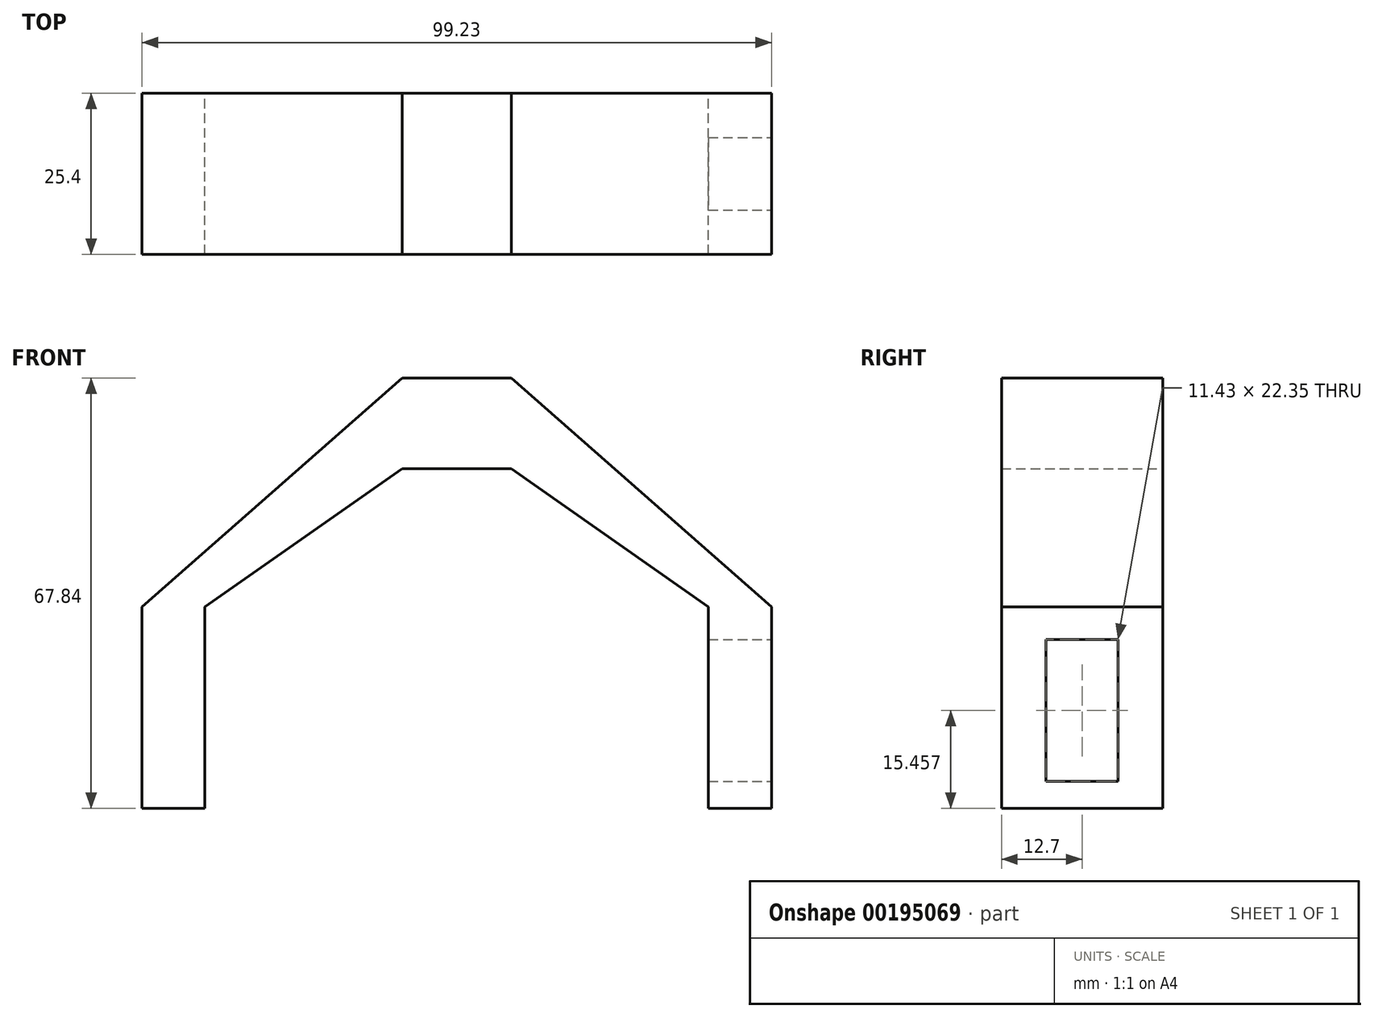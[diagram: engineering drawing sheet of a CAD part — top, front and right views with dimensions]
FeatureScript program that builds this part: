
annotation { "Feature Type Name" : "Feature", "Feature Type Description" : "" }
export const myFeature = defineFeature(function(context is Context, id is Id, definition is map)
    precondition{}
    {
        {
            var Q0;
            Q0=qCreatedBy(makeId("Front.planeOp"),FACE);
            var sketch = newSketch(context, id + "F0", { "sketchPlane" : qUnion([Q0])});
            skLineSegment(sketch, "E0.bottom", {"start": v(-126.2, 0) * mm, "end": v(-116.27, 0) * mm});
            skLineSegment(sketch, "E0.top", {"start": v(-126.2, 31.75) * mm, "end": v(-116.27, 31.75) * mm});
            skLineSegment(sketch, "E0.left", {"start": v(-126.2, 0) * mm, "end": v(-126.2, 31.75) * mm});
            skLineSegment(sketch, "E0.right", {"start": v(-116.27, 0) * mm, "end": v(-116.27, 31.75) * mm});
            skLineSegment(sketch, "E1.bottom", {"start": v(-26.96, 0) * mm, "end": v(-36.9, 0) * mm});
            skLineSegment(sketch, "E1.top", {"start": v(-26.96, 31.75) * mm, "end": v(-36.9, 31.75) * mm});
            skLineSegment(sketch, "E1.left", {"start": v(-26.96, 0) * mm, "end": v(-26.96, 31.75) * mm});
            skLineSegment(sketch, "E1.right", {"start": v(-36.9, 0) * mm, "end": v(-36.9, 31.75) * mm});
            skLineSegment(sketch, "E2", {"start": v(-126.2, 31.75) * mm, "end": v(-85.2, 67.84) * mm});
            skLineSegment(sketch, "E3", {"start": v(-85.2, 67.84) * mm, "end": v(-67.95, 67.84) * mm});
            skLineSegment(sketch, "E4", {"start": v(-67.95, 67.84) * mm, "end": v(-26.96, 31.75) * mm});
            skLineSegment(sketch, "E5", {"start": v(-36.9, 31.75) * mm, "end": v(-67.95, 53.57) * mm});
            skLineSegment(sketch, "E6", {"start": v(-67.95, 53.57) * mm, "end": v(-85.2, 53.57) * mm});
            skLineSegment(sketch, "E7", {"start": v(-85.2, 53.57) * mm, "end": v(-116.27, 31.75) * mm});
            skLineSegment(sketch, "E8", {"start": v(-85.2, 67.84) * mm, "end": v(-85.2, 53.57) * mm});
            skLineSegment(sketch, "E9", {"start": v(-67.95, 67.84) * mm, "end": v(-67.95, 53.57) * mm});
            skSolve(sketch);
        }
        {
            var Q0;
            Q0 = qSketchRegion(id + "F0", true);
            extrude(context, id + "F1", {"entities" : qUnion([Q0]), "depth" : 25.4 * mm});
        }
        {
            var Q0;
            Q0=makeQuery(id+"F1.opExtrude","SWEPT_FACE",FACE,{"disambiguationData":[OSD([sQuery(id+"F0.wireOp",EDGE,"E1.left")])]});
            var sketch = newSketch(context, id + "F2", { "sketchPlane" : qUnion([Q0])});
            skLineSegment(sketch, "E10.bottom", {"start": v(-18.42, 26.63) * mm, "end": v(-6.99, 26.63) * mm});
            skLineSegment(sketch, "E10.top", {"start": v(-18.42, 4.28) * mm, "end": v(-6.99, 4.28) * mm});
            skLineSegment(sketch, "E10.left", {"start": v(-18.42, 26.63) * mm, "end": v(-18.42, 4.28) * mm});
            skLineSegment(sketch, "E10.right", {"start": v(-6.99, 26.63) * mm, "end": v(-6.99, 4.28) * mm});
            skSolve(sketch);
        }
        {
            var Q0;
            Q0 = qSketchRegion(id + "F2", true);
            extrude(context, id + "F3", {"entities" : qUnion([Q0]), "operationType" : NewBodyOperationType.REMOVE, "oppositeDirection" : true, "depth" : 25.4 * mm});
        }
    });
